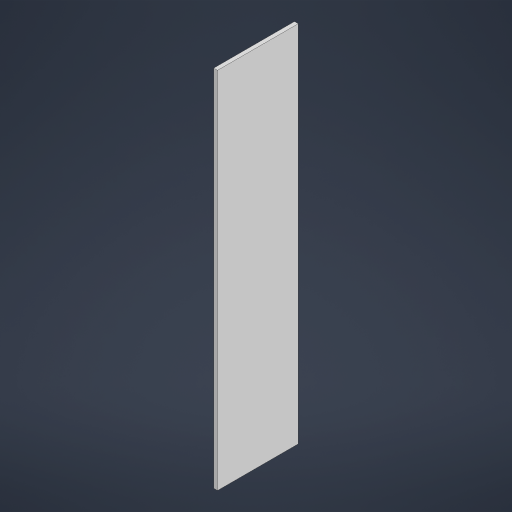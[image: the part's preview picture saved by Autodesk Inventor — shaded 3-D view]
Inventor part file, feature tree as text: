
AUTODESK INVENTOR PART (.ipt)
format: ipt  version: 2023 (Build 270158000, 158)  size: 166,400 bytes
history: native  units: mm
features: extrude x1, sketch x1
ambient origin geometry x8: Origin, YZ Plane, XZ Plane, XY Plane, X Axis, Y Axis, Z Axis, Center Point
bodies: Solid1 (feature_tree)
feature tree (2):
  extrude  "Extrusion1"  Depth=288.0mm
  sketch  "Sketch1"  dims[d0=63.9mm d1=288.0mm d2=3.0mm d3=0.0mm]
